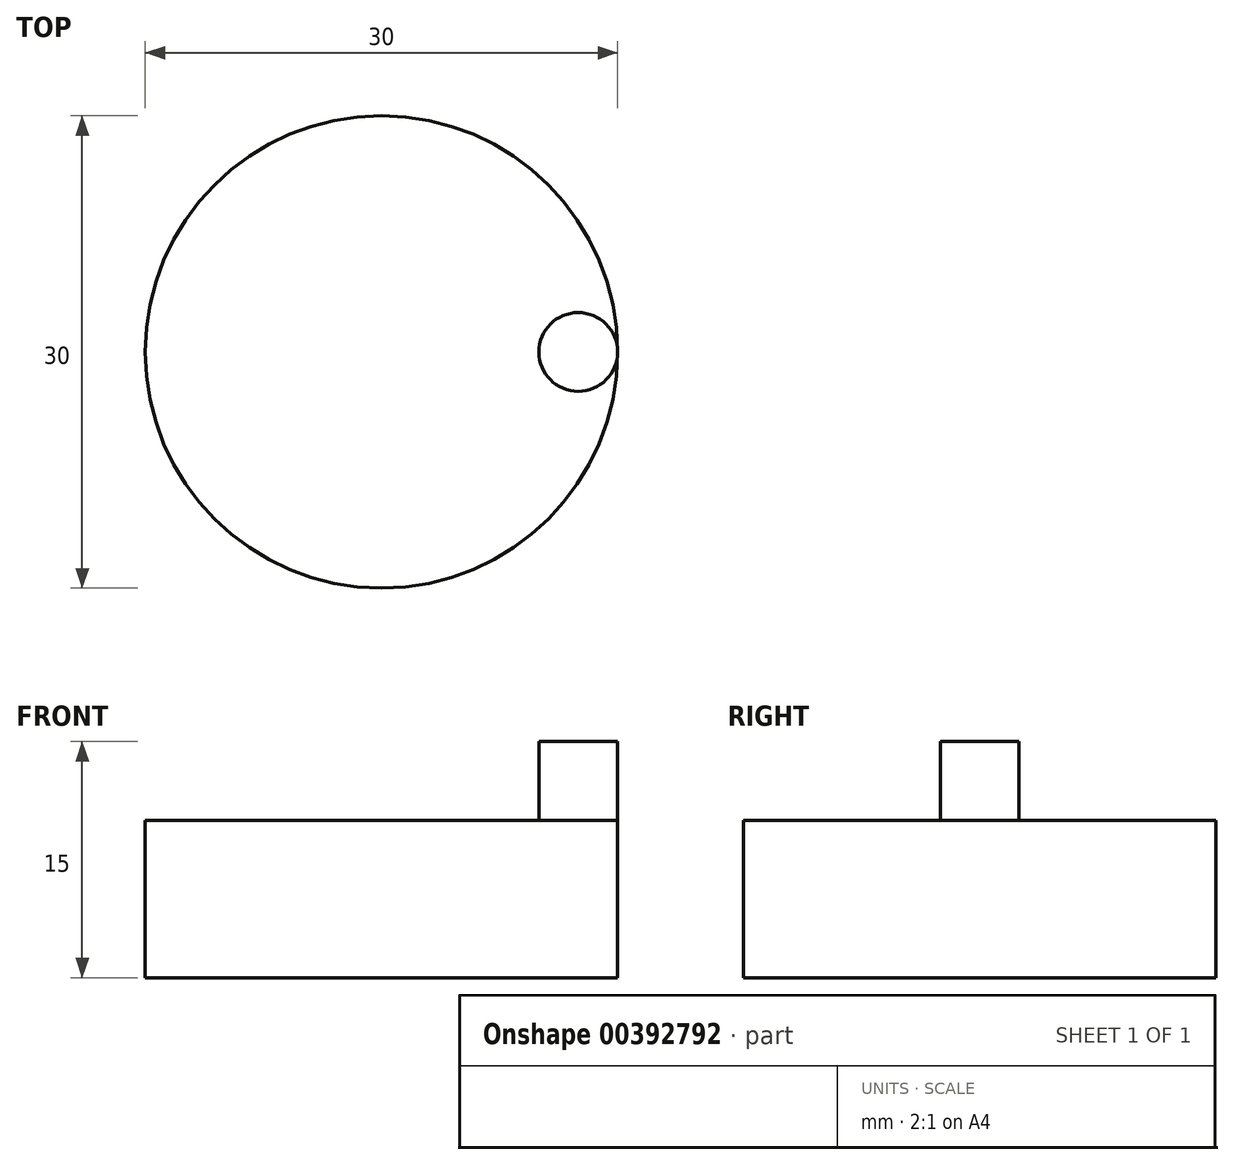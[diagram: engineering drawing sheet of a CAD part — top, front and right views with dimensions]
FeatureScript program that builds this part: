
annotation { "Feature Type Name" : "Feature", "Feature Type Description" : "" }
export const myFeature = defineFeature(function(context is Context, id is Id, definition is map)
    precondition{}
    {
        {
            var Q0;
            Q0=qCreatedBy(makeId("Top.planeOp"),FACE);
            var sketch = newSketch(context, id + "F0", { "sketchPlane" : qUnion([Q0])});
            skCircle(sketch, "E0", {"center": v(0, 0) * mm, "radius": 15 * mm});
            skSolve(sketch);
        }
        {
            var Q0;
            Q0 = qSketchRegion(id + "F0", true);
            extrude(context, id + "F1", {"entities" : qUnion([Q0]), "depth" : 10 * mm, "offsetDistance" : 25 * mm});
        }
        {
            var Q0;
            Q0=makeQuery(id+"F1.opExtrude","CAP_FACE",FACE,{"disambiguationData":[OSD([sQuery(id+"F0.wireOp",EDGE,"E0")])],"isStart":false});
            var sketch = newSketch(context, id + "F2", { "sketchPlane" : qUnion([Q0])});
            skLineSegment(sketch, "E1", {"start": v(0, 0) * mm, "end": v(15, 0) * mm, "construction": true});
            skPoint(sketch, "E2", {"position": v(12.5, 0) * mm});
            skCircle(sketch, "E3", {"center": v(12.5, 0) * mm, "radius": 2.5 * mm});
            skSolve(sketch);
        }
        {
            var Q0;
            Q0 = qSketchRegion(id + "F2", true);
            extrude(context, id + "F3", {"entities" : qUnion([Q0]), "operationType" : NewBodyOperationType.ADD, "depth" : 5 * mm, "offsetDistance" : 25 * mm});
        }
    });
